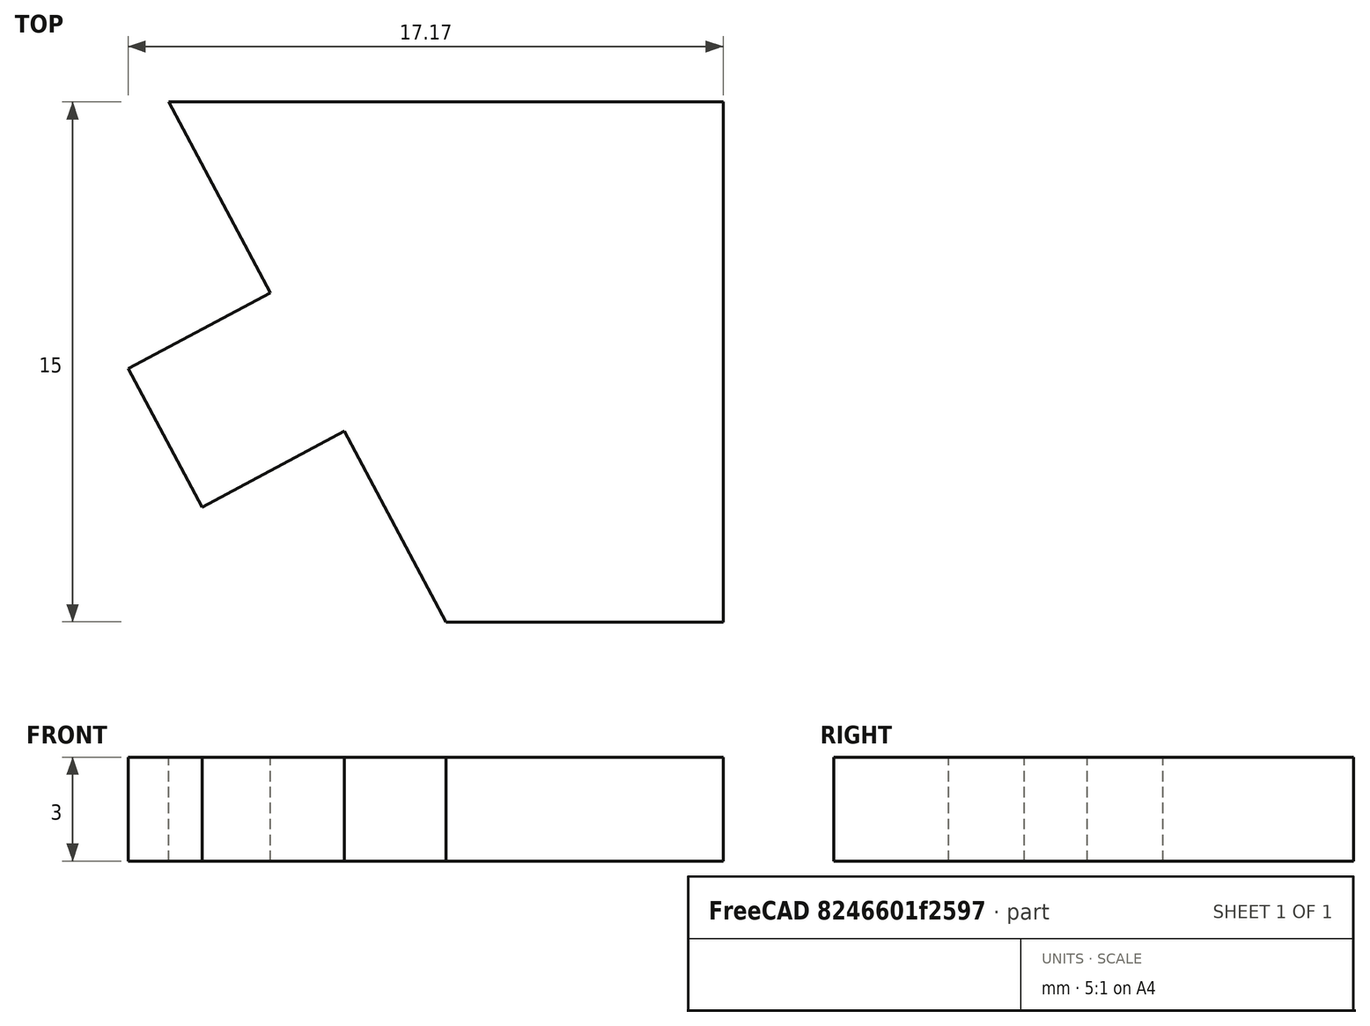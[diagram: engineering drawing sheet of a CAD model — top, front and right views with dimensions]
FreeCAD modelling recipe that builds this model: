
FCSTD DOCUMENT  (FreeCAD 0.19R22960 (Git))
Label: draft1
License: All rights reserved
LicenseURL: http://en.wikipedia.org/wiki/All_rights_reserved
objects: Sketcher::SketchObject×1, PartDesign::Pad×1, PartDesign::Body×1
note: 4 computed .brp shape members not serialized (recipe doc carries the construction recipe); baked Part::Feature solids carry a one-line shape summary decoded from their .brp

FEATURE [Sketcher::SketchObject] Sketch
  MapMode = 5
  Support = -> [XY_Plane]
  sketch-geometry (8):
    g0: LineSegment StartX=-28.9834 StartY=33.3517 StartZ=0 EndX=-36.9834 EndY=33.3517 EndZ=0
    g1: LineSegment StartX=-39.9895 StartY=39.5517 StartZ=0 EndX=-44.0895 EndY=37.5638 EndZ=0
    g2: LineSegment StartX=-44.0895 StartY=37.5638 StartZ=0 EndX=-46.0773 EndY=41.6638 EndZ=0
    g3: LineSegment StartX=-46.0773 StartY=41.6638 StartZ=0 EndX=-41.9773 EndY=43.6517 EndZ=0
    g4: LineSegment StartX=-41.9773 StartY=43.6517 StartZ=0 EndX=-44.9834 EndY=49.8517 EndZ=0
    g5: LineSegment StartX=-44.9834 StartY=49.8517 StartZ=0 EndX=-28.9834 EndY=49.8517 EndZ=0
    g6: LineSegment StartX=-28.9834 StartY=49.8517 StartZ=0 EndX=-28.9834 EndY=33.3517 EndZ=0
    g7: LineSegment StartX=-36.9834 StartY=33.3517 StartZ=0 EndX=-39.9895 EndY=39.5517 EndZ=0
  constraints (22):
    c: Coincident(g1,g2)
    c: Coincident(g2,g3)
    c: Coincident(g3,g4)
    c: Coincident(g5,g6)
    c: Coincident(g4,g5)
    c: Coincident(g0,g6)
    c: DistanceX(g0,g0) = 8
    c: DistanceY(g6,g6) = 16.5
    c: Vertical(g6)
    c: Horizontal(g5)
    c: Horizontal(g0)
    c: Coincident(g1,g7)
    c: Coincident(g0,g7)
    c: Equal(g4,g7)
    c: DistanceX(g5,g5) = 16
    c: Angle(g1,g2) = 1.5708
    c: Equal(g3,g1)
    c: DistanceY(g2,g2) = 4.1
    c: DistanceX(g3,g3) = 4.1
    c: Angle(g4,g3) = 1.5708
    c: Angle(g1,g7) = 1.5708
    c: Angle(g2,g3) = 1.5708
FEATURE [PartDesign::Pad] Pad
  Direction = (1,1,1)
  Length = 3
  Length2 = 100
  Profile = -> Sketch
  Type = 0
FEATURE [PartDesign::Body] Body
  Group = -> [Sketch,Pad]
  Origin = -> Origin
  Tip = -> Pad
